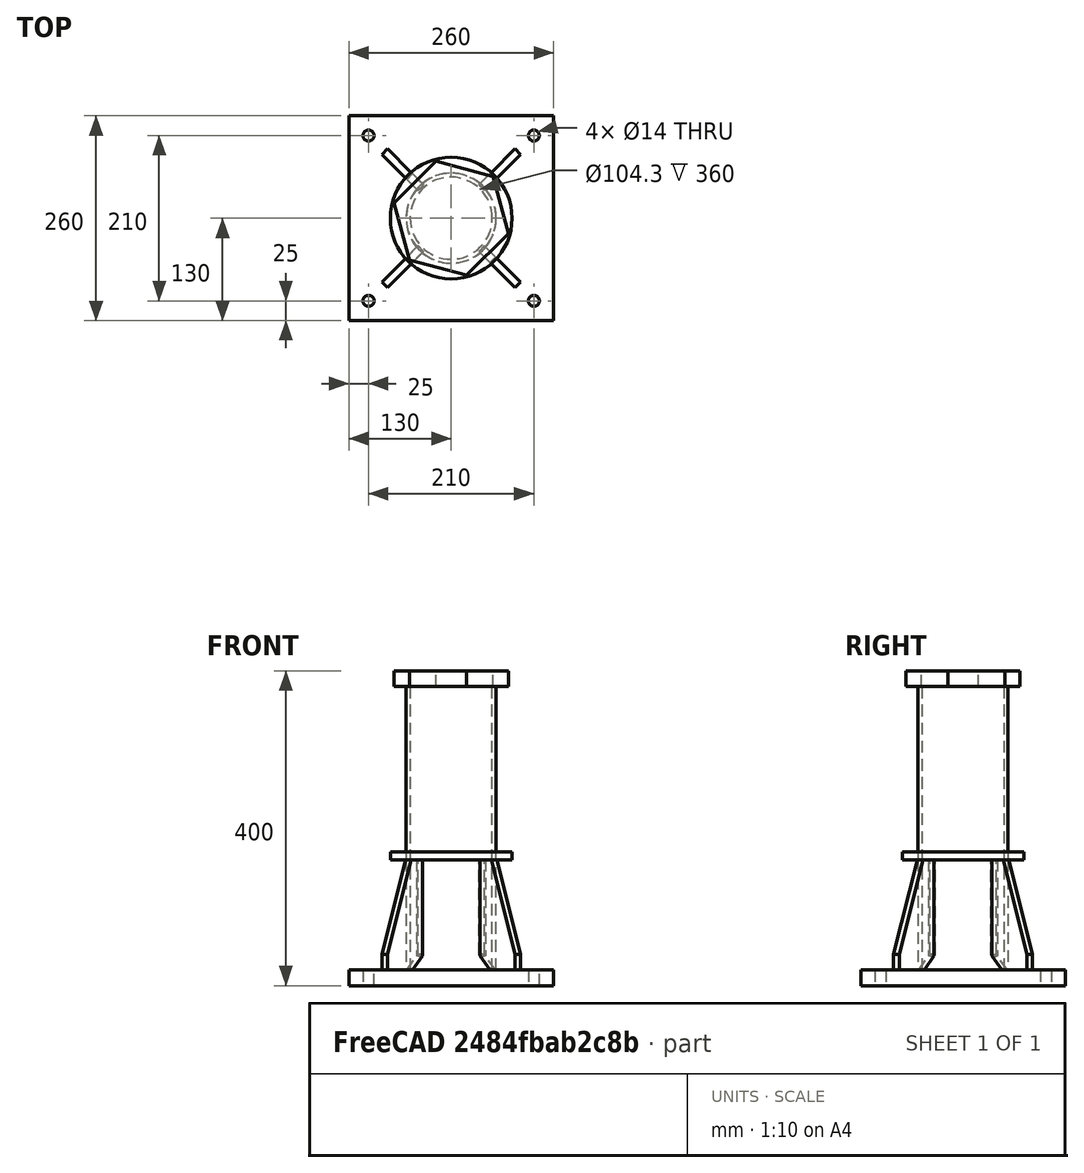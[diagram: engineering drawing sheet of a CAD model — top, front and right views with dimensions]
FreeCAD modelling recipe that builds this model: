
FCSTD DOCUMENT  (FreeCAD 0.21R33694 (Git))
Label: Wyk_Rohrstoss_ring
License: All rights reserved
LicenseURL: http://en.wikipedia.org/wiki/All_rights_reserved
objects: Sketcher::SketchObject×4, Part::Extrusion×4, Part::FeaturePython×3, Fem::ConstraintForce×3, Fem::FemSolverObjectPython×1, App::MaterialObjectPython×1, Part::Revolution×1, Fem::ConstraintFixed×1, Fem::FemMeshObjectPython×1, Fem::FemAnalysis×1
note: 12 computed .brp shape members not serialized (recipe doc carries the construction recipe); baked Part::Feature solids carry a one-line shape summary decoded from their .brp

FEATURE [Sketcher::SketchObject] Sketch
  FullyConstrained = true
  sketch-geometry (12):
    g0: LineSegment StartX=-130 StartY=130 StartZ=0 EndX=130 EndY=130 EndZ=0
    g1: LineSegment StartX=130 StartY=130 StartZ=0 EndX=130 EndY=-130 EndZ=0
    g2: LineSegment StartX=130 StartY=-130 StartZ=0 EndX=-130 EndY=-130 EndZ=0
    g3: LineSegment StartX=-130 StartY=-130 StartZ=0 EndX=-130 EndY=130 EndZ=0
    g4: LineSegment StartX=-105 StartY=105 StartZ=0 EndX=105 EndY=105 EndZ=0
    g5: LineSegment StartX=105 StartY=105 StartZ=0 EndX=105 EndY=-105 EndZ=0
    g6: LineSegment StartX=105 StartY=-105 StartZ=0 EndX=-105 EndY=-105 EndZ=0
    g7: LineSegment StartX=-105 StartY=-105 StartZ=0 EndX=-105 EndY=105 EndZ=0
    g8: Circle CenterX=-105 CenterY=105 CenterZ=0 NormalX=0 NormalY=0 NormalZ=1 AngleXU=0 Radius=7
    g9: Circle CenterX=105 CenterY=105 CenterZ=0 NormalX=0 NormalY=0 NormalZ=1 AngleXU=0 Radius=7
    g10: Circle CenterX=-105 CenterY=-105 CenterZ=0 NormalX=0 NormalY=0 NormalZ=1 AngleXU=0 Radius=7
    g11: Circle CenterX=105 CenterY=-105 CenterZ=0 NormalX=0 NormalY=0 NormalZ=1 AngleXU=0 Radius=7
  constraints (28):
    c: Coincident(g0,g1)
    c: Coincident(g1,g2)
    c: Coincident(g2,g3)
    c: Coincident(g3,g0)
    c: Horizontal(g0)
    c: Vertical(g1)
    c: Symmetric(g2,g1,g-2)
    c: Symmetric(g2,g0,g-1)
    c: Equal(g2,g3)
    c: DistanceX(g2,g2) = 260
    c: Coincident(g4,g5)
    c: Coincident(g5,g6)
    c: Coincident(g6,g7)
    c: Coincident(g7,g4)
    c: Horizontal(g4)
    c: Vertical(g7)
    c: Symmetric(g5,g4,g-1)
    c: Symmetric(g6,g5,g-2)
    c: Equal(g6,g5)
    c: DistanceX(g6,g6) = 210
    c: Coincident(g8,g4)
    c: Coincident(g9,g4)
    c: Coincident(g10,g6)
    c: Coincident(g11,g5)
    c: Equal(g8,g9)
    c: Equal(g8,g11)
    c: Equal(g8,g10)
    c: Diameter(g8) = 14
FEATURE [Part::Extrusion] Extrude  label="platte"
  Base = -> Sketch
  Dir = (0,0,1)
  DirMode = 2
  FaceMakerClass = Part::FaceMakerBullseye
  LengthFwd = 20
  LengthRev = 0
  Solid = true
  Symmetric = false
FEATURE [Sketcher::SketchObject] Sketch001
  FullyConstrained = true
  MapMode = 5
  Placement = pos=(0,0,20) rot=(0,0,1;0rad)
  Support = -> [Extrude]
  sketch-geometry (3):
    g0: Circle CenterX=0 CenterY=0 CenterZ=0 NormalX=0 NormalY=0 NormalZ=1 AngleXU=0 Radius=57.15
    g1: Circle CenterX=0 CenterY=0 CenterZ=0 NormalX=0 NormalY=0 NormalZ=1 AngleXU=0 Radius=52.15
    g2: LineSegment StartX=52.15 StartY=0 StartZ=0 EndX=57.15 EndY=0 EndZ=0
  constraints (8):
    c: Coincident(g0,g-1)
    c: Coincident(g1,g0)
    c: Diameter(g0) = 114.3
    c: PointOnObject(g2,g1)
    c: PointOnObject(g2,g0)
    c: PointOnObject(g2,g-1)
    c: Horizontal(g2)
    c: DistanceX(g2,g2) = 5
FEATURE [Part::Extrusion] Extrude001  label="R114x5"
  Base = -> Sketch001
  Dir = (0,0,1)
  DirMode = 2
  FaceMakerClass = Part::FaceMakerBullseye
  LengthFwd = 360
  LengthRev = 0
  Solid = true
  Symmetric = false
FEATURE [Sketcher::SketchObject] Sketch002
  ExternalGeometry = -> [Extrude]
  FullyConstrained = true
  Placement = pos=(0,0,0) rot=(1,0,0;1.5708rad)
  sketch-geometry (6):
    g0: LineSegment StartX=54.65 StartY=160 StartZ=0 EndX=77.15 EndY=160 EndZ=0
    g1: LineSegment StartX=77.15 StartY=160 StartZ=0 EndX=119.65 EndY=40 EndZ=0
    g2: LineSegment StartX=119.65 StartY=40 StartZ=0 EndX=119.65 EndY=20 EndZ=0
    g3: LineSegment StartX=119.65 StartY=20 StartZ=0 EndX=74.65 EndY=20 EndZ=0
    g4: LineSegment StartX=74.65 StartY=20 StartZ=0 EndX=54.65 EndY=40 EndZ=0
    g5: LineSegment StartX=54.65 StartY=40 StartZ=0 EndX=54.65 EndY=160 EndZ=0
  constraints (18):
    c: Horizontal(g0)
    c: Coincident(g0,g1)
    c: Coincident(g1,g2)
    c: Vertical(g2)
    c: Coincident(g2,g3)
    c: Coincident(g3,g4)
    c: Coincident(g4,g5)
    c: Coincident(g5,g0)
    c: Vertical(g5)
    c: Horizontal(g3)
    c: Horizontal(g2,g-3)
    c: DistanceY(g3,g4) = 20
    c: DistanceX(g4,g3) = 20
    c: DistanceX(g4,g2) = 65
    c: DistanceY(g2,g2) = 20
    c: DistanceX(g-1,g4) = 54.65
    c: DistanceX(g0,g0) = 22.5
    c: DistanceY(g2,g0) = 140
FEATURE [Part::Extrusion] Extrude002
  Base = -> Sketch002
  Dir = (0,-1,2e-16)
  DirMode = 2
  FaceMakerClass = Part::FaceMakerBullseye
  LengthFwd = 10
  LengthRev = 0
  Solid = true
  Symmetric = true
FEATURE [Part::FeaturePython] Array  label="steifen"  # Draft array (typed FeaturePython)
  Angle = 360
  ArrayType = 1
  Axis = (0,0,1)
  Base = -> Extrude002
  Center = (0,0,0)
  Count = 4
  Fuse = false
  IntervalAxis = (0,0,0)
  IntervalX = (50,0,0)
  IntervalY = (0,50,0)
  IntervalZ = (0,0,50)
  NumberCircles = 3
  NumberPolar = 4
  NumberX = 2
  NumberY = 2
  NumberZ = 1
  Placement = pos=(0,0,0) rot=(0,0,1;0.785398rad)
  RadialDistance = 50
  Symmetry = 1
  TangentialDistance = 25
FEATURE [Sketcher::SketchObject] Sketch003
  FullyConstrained = true
  MapMode = 5
  Placement = pos=(0,0,380) rot=(0,0,1;0rad)
  Support = -> [Extrude001]
  sketch-geometry (8):
    g0: LineSegment StartX=72.4981 StartY=-19.4258 StartZ=0 EndX=53.0723 EndY=53.0723 EndZ=0
    g1: LineSegment StartX=53.0723 StartY=53.0723 StartZ=0 EndX=-19.4258 EndY=72.4981 EndZ=0
    g2: LineSegment StartX=-19.4258 StartY=72.4981 StartZ=0 EndX=-72.4981 EndY=19.4258 EndZ=0
    g3: LineSegment StartX=-72.4981 StartY=19.4258 StartZ=0 EndX=-53.0723 EndY=-53.0723 EndZ=0
    g4: LineSegment StartX=-53.0723 StartY=-53.0723 StartZ=0 EndX=19.4258 EndY=-72.4981 EndZ=0
    g5: LineSegment StartX=19.4258 StartY=-72.4981 StartZ=0 EndX=72.4981 EndY=-19.4258 EndZ=0
    g6: Circle CenterX=0 CenterY=0 CenterZ=0 NormalX=0 NormalY=0 NormalZ=1 AngleXU=0 Radius=75.0555
    g7: LineSegment StartX=0 StartY=0 StartZ=0 EndX=45.9619 EndY=-45.9619 EndZ=0
  constraints (18):
    c: Coincident(g0,g1)
    c: Coincident(g1,g2)
    c: Coincident(g2,g3)
    c: Coincident(g3,g4)
    c: Coincident(g4,g5)
    c: Coincident(g5,g0)
    c: Equal(g0, g1-g5) x5
    c: PointOnObject(g0,g6)
    c: PointOnObject(g1,g6)
    c: PointOnObject(g2,g6)
    c: PointOnObject(g3,g6)
    c: PointOnObject(g4,g6)
    c: Coincident(g6,g-1)
    c: Coincident(g7,g6)
    c: PointOnObject(g7,g5)
    c: Symmetric(g4,g0,g7)
    c: Angle(g7,g-1) = 0.785398
    c: Distance(g1,g0) = 130
FEATURE [Part::Extrusion] Extrude003  label="lastplatte"
  Base = -> Sketch003
  Dir = (0,0,1)
  DirMode = 2
  FaceMakerClass = Part::FaceMakerBullseye
  LengthFwd = 20
  LengthRev = 0
  Solid = true
  Symmetric = false
FEATURE [Fem::FemSolverObjectPython] SolverCcxTools  # FEM object (typed FeaturePython)
  AnalysisType = 0
  BeamShellResultOutput3D = true
  BucklingFactors = 1
  EigenmodeHighLimit = 1000000
  EigenmodeLowLimit = 0
  EigenmodesCount = 10
  GeometricalNonlinearity = 0
  IterationsControlParameterCutb = 0.25,0.5,0.75,0.85,,,1.5,
  IterationsControlParameterIter = 4,8,9,200,10,400,,200,,
  IterationsControlParameterTimeUse = false
  IterationsThermoMechMaximum = 2000
  IterationsUserDefinedIncrementations = false
  IterationsUserDefinedTimeStepLength = false
  MaterialNonlinearity = 0
  MatrixSolverType = 1
  SplitInputWriter = true
  ThermoMechSteadyState = true
  TimeEnd = 1
  TimeInitialStep = 0.01
FEATURE [App::MaterialObjectPython] MaterialSolid  label="S235"  # material (typed FeaturePython)
  Category = 0
  Material = AuthorAndLicense=(c) 2013 Juergen Riegel (CC-BY 3.0),CardName=CalculiX-Steel,Density=7900 kg/m^3,+8 more (map truncated)
FEATURE [Part::FeaturePython] Facebinder001  # WARN: FeaturePython — macro-defined, semantics opaque (R4)
  Area = 202.191
  Extrusion = 0
  RemoveSplitter = false
  Sew = false
FEATURE [Part::Revolution] Revolve
  Angle = 360
  Axis = (0,0,1)
  Base = (0,0,0)
  FaceMakerClass = Part::FaceMakerBullseye
  Solid = false
  Source = -> Facebinder001
  Symmetric = false
FEATURE [Part::FeaturePython] BooleanFragments  # WARN: FeaturePython — macro-defined, semantics opaque (R4)
  Mode = 2
  Objects = -> [Extrude,Extrude001,Array,Extrude003,Revolve]
  Tolerance = 0
FEATURE [Fem::ConstraintFixed] ConstraintFixed
  NormalDirection = (1,-1e-16,0)
  Normals = (48) [(-1,0,0),(0.5,-0.866025,0),(0.5,0.866025,0),(-1,2.44929e-16,0),(-1,0,0),(0.5,-0.866025,0),(0.5,0.866025,0),(-1,2.44929e-16,0),(-1,0,0),+39 more]
  Points = (48) [(112,105,20),(101.5,111.062,20),(101.5,98.9378,20),(112,105,20),(112,105,10),(101.5,111.062,10),(101.5,98.9378,10),(112,105,10),(112,105,0),+39 more]
  References = -> [BooleanFragments]
  Scale = 4
FEATURE [Fem::ConstraintForce] ConstraintForce
  Direction = -> BooleanFragments [Edge112]
  DirectionVector = (0,0,1)
  Force = 65330
  NormalDirection = (-0.707107,0.707107,0)
  Points = (12) [(-19.4258,72.4981,400),(-37.1166,54.8073,400),(-54.8073,37.1166,400),(-72.4981,19.4258,400),(-19.4258,72.4981,390),(-37.1166,54.8073,390),+6 more]
  References = -> [BooleanFragments]
  Scale = 6
FEATURE [Fem::ConstraintForce] ConstraintForce001
  Direction = -> BooleanFragments [Edge118]
  DirectionVector = (0,0,-1)
  Force = 65330
  NormalDirection = (0.707107,-0.707107,0)
  Points = (12) [(19.4258,-72.4981,400),(37.1166,-54.8073,400),(54.8073,-37.1166,400),(72.4981,-19.4258,400),(19.4258,-72.4981,390),(37.1166,-54.8073,390),+6 more]
  References = -> [BooleanFragments]
  Reversed = true
  Scale = 6
FEATURE [Fem::ConstraintForce] ConstraintForce002
  Direction = -> BooleanFragments [Edge33]
  DirectionVector = (0.707107,-0.707107,0)
  Force = 4410
  NormalDirection = (0,0,1)
  Points = (4) [(24.166,-24.166,400),(24.166,24.166,400),(-24.166,-24.166,400),(-24.166,24.166,400)]
  References = -> [BooleanFragments]
  Scale = 12
FEATURE [Fem::FemMeshObjectPython] FEMMeshGmsh  # FEM object (typed FeaturePython)
  Algorithm2D = 0
  Algorithm3D = 0
  CharacteristicLengthMax = 8
  CharacteristicLengthMin = 0
  CoherenceMesh = true
  ElementDimension = 0
  ElementOrder = 1
  GeometryTolerance = 1e-06
  GroupsOfNodes = false
  HighOrderOptimize = 0
  MeshSizeFromCurvature = 12
  OptimizeNetgen = false
  OptimizeStd = true
  Part = -> BooleanFragments
  RecombinationAlgorithm = 0
  Recombine3DAll = false
  RecombineAll = false
  SecondOrderLinear = false
FEATURE [Fem::FemAnalysis] Analysis
  Group = -> [SolverCcxTools,MaterialSolid,ConstraintFixed,ConstraintForce,ConstraintForce001,ConstraintForce002,FEMMeshGmsh]
